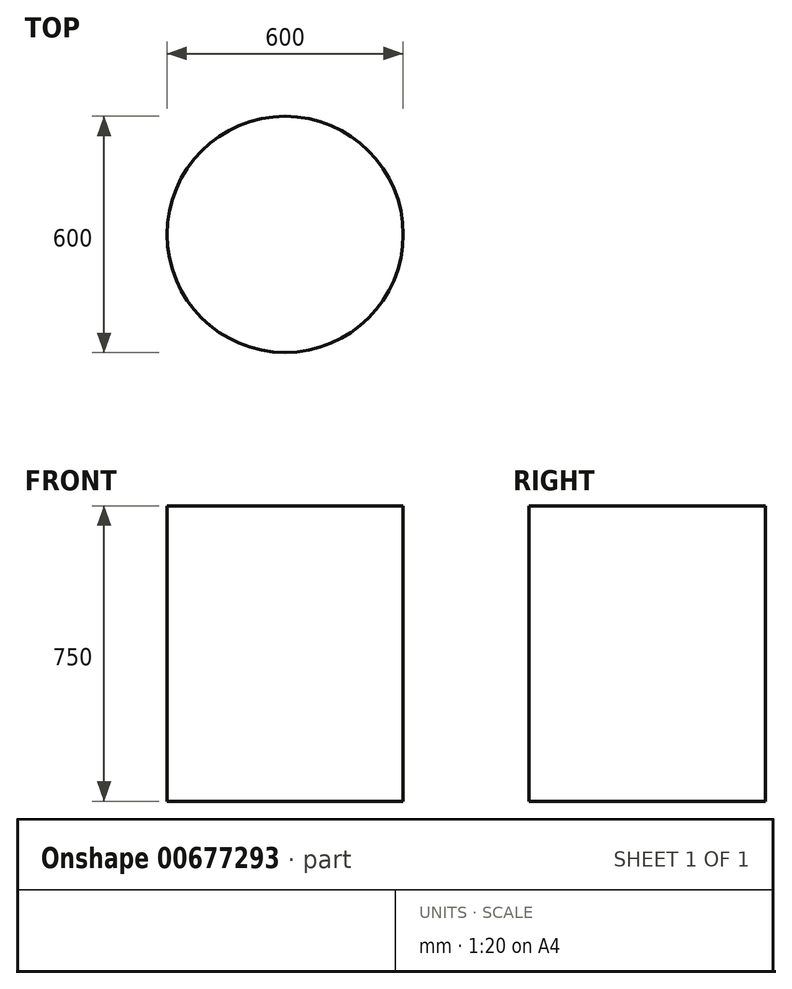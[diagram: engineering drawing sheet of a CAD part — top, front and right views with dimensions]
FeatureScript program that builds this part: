
annotation { "Feature Type Name" : "Feature", "Feature Type Description" : "" }
export const myFeature = defineFeature(function(context is Context, id is Id, definition is map)
    precondition{}
    {
        {
            var Q0;
            Q0=qCreatedBy(makeId("Top.planeOp"),FACE);
            var sketch = newSketch(context, id + "F0", { "sketchPlane" : qUnion([Q0])});
            skCircle(sketch, "E0", {"center": v(0, 0) * mm, "radius": 300 * mm});
            skSolve(sketch);
        }
        {
            var Q0;
            Q0=makeQuery(id+"F0.imprint","IMPRINT",FACE,{"disambiguationData":[TD([[makeQuery(id+"F0.imprint","IMPRINT",EDGE,{"derivedFrom":sQuery(id+"F0.wireOp",EDGE,"E0")}),1.0]])]});
            extrude(context, id + "F1", {"entities" : qUnion([Q0]), "depth" : 750 * mm, "offsetDistance" : 25 * mm});
        }
        {
            var Q0;
            Q0=qCreatedBy(makeId("Right.planeOp"),FACE);
            var sketch = newSketch(context, id + "F2", { "sketchPlane" : qUnion([Q0])});
            skLineSegment(sketch, "E1", {"start": v(457.4, 426.88) * mm, "end": v(-420.32, 191.7) * mm});
            skSolve(sketch);
        }
        {
            var Q0;
            Q0 = qSketchRegion(id + "F2", true);
            var Q1;
            Q1=sQuery(id+"F2.wireOp",EDGE,"E1");
            extrude(context, id + "F3", {"entities" : qUnion([Q0]), "bodyType" : ToolBodyType.SURFACE, "surfaceEntities" : qUnion([Q1]), "endBound" : BoundingType.SYMMETRIC, "oppositeDirection" : true, "depth" : 700 * mm, "offsetDistance" : 25 * mm});
        }
    });
